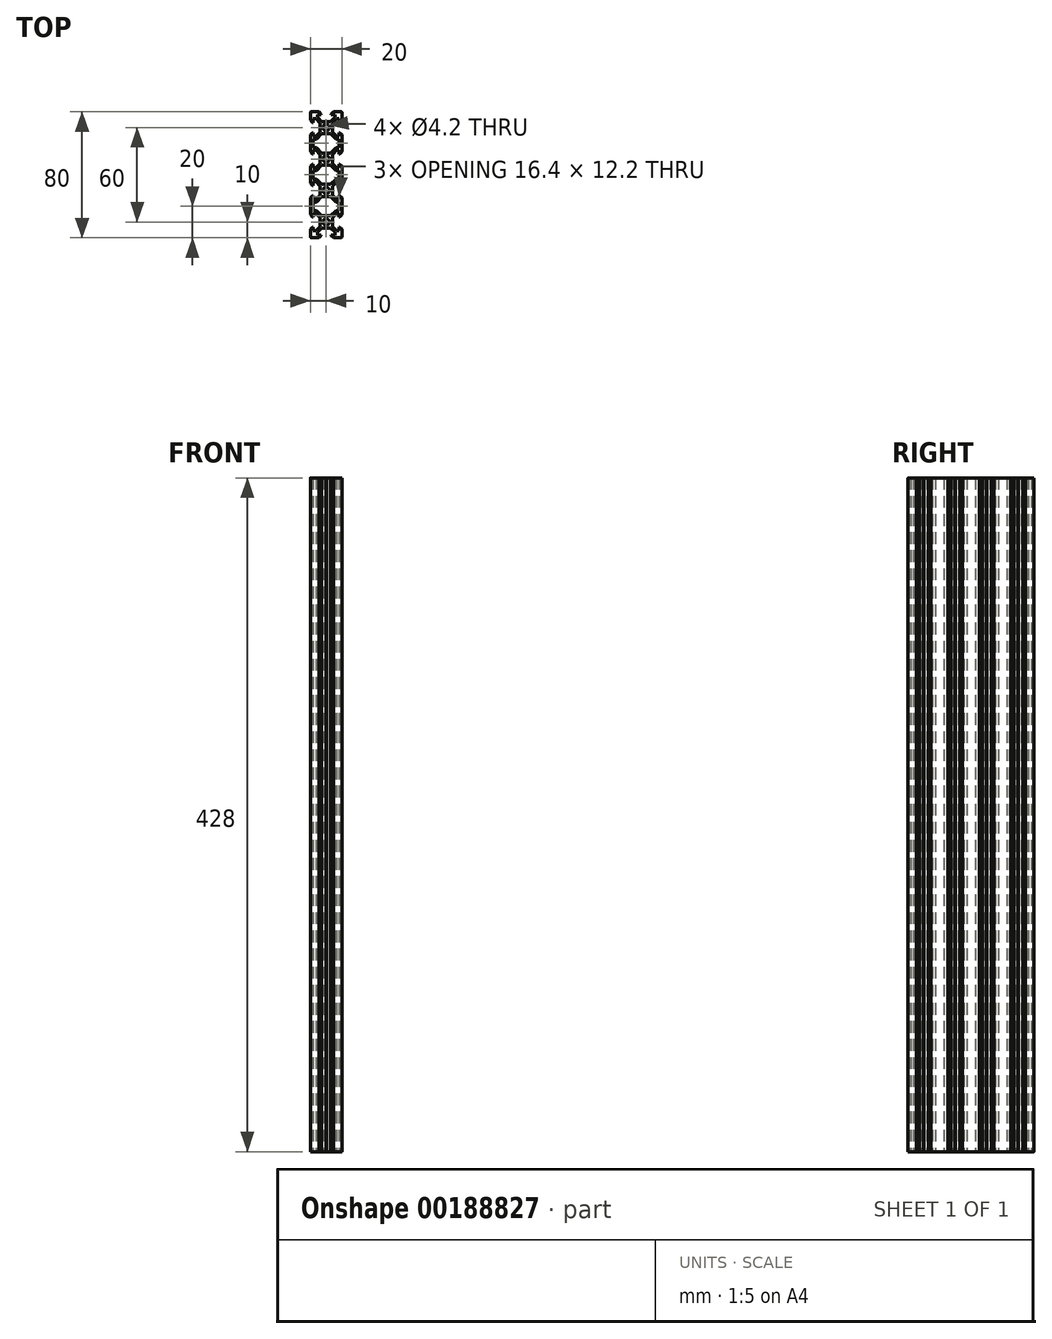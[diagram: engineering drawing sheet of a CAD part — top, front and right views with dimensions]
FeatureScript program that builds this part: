
annotation { "Feature Type Name" : "Feature", "Feature Type Description" : "" }
export const myFeature = defineFeature(function(context is Context, id is Id, definition is map)
    precondition{}
    {
        {
            assignVariable(context, id + "F0", {"name" : "altezza", "anyValue" : 428});
        }
        {
            var Q0;
            Q0=qCreatedBy(makeId("Top.planeOp"),FACE);
            var sketch = newSketch(context, id + "F1", { "sketchPlane" : qUnion([Q0])});
            skArc(sketch, "E0", {"start": v(-2.1, -10) * mm, "mid": v(0, -12.1) * mm, "end": v(2.1, -10) * mm});
            skArc(sketch, "E1", {"start": v(-2.1, -30) * mm, "mid": v(0, -32.1) * mm, "end": v(2.1, -30) * mm});
            skArc(sketch, "E2", {"start": v(-2.1, 30) * mm, "mid": v(0, 27.9) * mm, "end": v(2.1, 30) * mm});
            skArc(sketch, "E3", {"start": v(-2.1, 10) * mm, "mid": v(0, 7.9) * mm, "end": v(2.1, 10) * mm});
            skLineSegment(sketch, "E4", {"start": v(3.69, 30) * mm, "end": v(3.9, 29.79) * mm});
            skLineSegment(sketch, "E5", {"start": v(3.69, 30) * mm, "end": v(3.9, 30.21) * mm});
            skLineSegment(sketch, "E6", {"start": v(3.9, 30.21) * mm, "end": v(3.9, 32.84) * mm});
            skLineSegment(sketch, "E7", {"start": v(3.9, 32.84) * mm, "end": v(6.56, 35.5) * mm});
            skLineSegment(sketch, "E8", {"start": v(6.56, 35.5) * mm, "end": v(8.2, 35.5) * mm});
            skLineSegment(sketch, "E9", {"start": v(8.2, 35.5) * mm, "end": v(8.2, 33.12) * mm});
            skLineSegment(sketch, "E10", {"start": v(8.2, 33.12) * mm, "end": v(8.54, 33.12) * mm});
            skLineSegment(sketch, "E11", {"start": v(8.54, 33.12) * mm, "end": v(10, 34.58) * mm});
            skLineSegment(sketch, "E12", {"start": v(10, 34.58) * mm, "end": v(10, 39.5) * mm});
            skArc(sketch, "E13", {"start": v(10, 39.5) * mm, "mid": v(9.85, 39.85) * mm, "end": v(9.5, 40) * mm});
            skLineSegment(sketch, "E14", {"start": v(9.5, 40) * mm, "end": v(4.58, 40) * mm});
            skLineSegment(sketch, "E15", {"start": v(3.12, 38.55) * mm, "end": v(4.58, 40) * mm});
            skLineSegment(sketch, "E16", {"start": v(3.12, 38.2) * mm, "end": v(3.12, 38.55) * mm});
            skLineSegment(sketch, "E17", {"start": v(5.5, 38.2) * mm, "end": v(3.12, 38.2) * mm});
            skLineSegment(sketch, "E18", {"start": v(5.5, 36.56) * mm, "end": v(5.5, 38.2) * mm});
            skLineSegment(sketch, "E19", {"start": v(2.84, 33.9) * mm, "end": v(5.5, 36.56) * mm});
            skLineSegment(sketch, "E20", {"start": v(0.21, 33.9) * mm, "end": v(2.84, 33.9) * mm});
            skLineSegment(sketch, "E21", {"start": v(0, 33.69) * mm, "end": v(0.2, 33.9) * mm});
            skLineSegment(sketch, "E22", {"start": v(0, 33.69) * mm, "end": v(-0.2, 33.9) * mm});
            skLineSegment(sketch, "E23", {"start": v(-0.21, 33.9) * mm, "end": v(-2.84, 33.9) * mm});
            skLineSegment(sketch, "E24", {"start": v(-2.84, 33.9) * mm, "end": v(-5.5, 36.56) * mm});
            skLineSegment(sketch, "E25", {"start": v(-5.5, 36.56) * mm, "end": v(-5.5, 38.2) * mm});
            skLineSegment(sketch, "E26", {"start": v(-5.5, 38.2) * mm, "end": v(-3.12, 38.2) * mm});
            skLineSegment(sketch, "E27", {"start": v(-3.12, 38.2) * mm, "end": v(-3.12, 38.55) * mm});
            skLineSegment(sketch, "E28", {"start": v(-3.12, 38.55) * mm, "end": v(-4.58, 40) * mm});
            skLineSegment(sketch, "E29", {"start": v(-4.58, 40) * mm, "end": v(-9.5, 40) * mm});
            skArc(sketch, "E30", {"start": v(-9.5, 40) * mm, "mid": v(-9.85, 39.85) * mm, "end": v(-10, 39.5) * mm});
            skLineSegment(sketch, "E31", {"start": v(-10, 34.58) * mm, "end": v(-10, 39.5) * mm});
            skLineSegment(sketch, "E32", {"start": v(-8.54, 33.12) * mm, "end": v(-10, 34.58) * mm});
            skLineSegment(sketch, "E33", {"start": v(-8.2, 33.12) * mm, "end": v(-8.54, 33.12) * mm});
            skLineSegment(sketch, "E34", {"start": v(-8.2, 35.5) * mm, "end": v(-8.2, 33.12) * mm});
            skLineSegment(sketch, "E35", {"start": v(-6.56, 35.5) * mm, "end": v(-8.2, 35.5) * mm});
            skLineSegment(sketch, "E36", {"start": v(-3.9, 32.84) * mm, "end": v(-6.56, 35.5) * mm});
            skLineSegment(sketch, "E37", {"start": v(-3.9, 30.21) * mm, "end": v(-3.9, 32.84) * mm});
            skLineSegment(sketch, "E38", {"start": v(-3.69, 30) * mm, "end": v(-3.9, 30.21) * mm});
            skLineSegment(sketch, "E39", {"start": v(-3.69, 30) * mm, "end": v(-3.9, 29.79) * mm});
            skLineSegment(sketch, "E40", {"start": v(-3.9, 29.79) * mm, "end": v(-3.9, 27.16) * mm});
            skLineSegment(sketch, "E41", {"start": v(-3.9, 27.16) * mm, "end": v(-6.56, 24.5) * mm});
            skLineSegment(sketch, "E42", {"start": v(-6.56, 24.5) * mm, "end": v(-8.2, 24.5) * mm});
            skLineSegment(sketch, "E43", {"start": v(-8.2, 24.5) * mm, "end": v(-8.2, 26.88) * mm});
            skLineSegment(sketch, "E44", {"start": v(-8.2, 26.88) * mm, "end": v(-8.54, 26.88) * mm});
            skLineSegment(sketch, "E45", {"start": v(-8.54, 26.88) * mm, "end": v(-10, 25.42) * mm});
            skLineSegment(sketch, "E46", {"start": v(-10, 14.58) * mm, "end": v(-10, 25.42) * mm});
            skLineSegment(sketch, "E47", {"start": v(-8.54, 13.12) * mm, "end": v(-10, 14.58) * mm});
            skLineSegment(sketch, "E48", {"start": v(-8.2, 13.12) * mm, "end": v(-8.54, 13.12) * mm});
            skLineSegment(sketch, "E49", {"start": v(-8.2, 15.5) * mm, "end": v(-8.2, 13.12) * mm});
            skLineSegment(sketch, "E50", {"start": v(-6.56, 15.5) * mm, "end": v(-8.2, 15.5) * mm});
            skLineSegment(sketch, "E51", {"start": v(-3.9, 12.84) * mm, "end": v(-6.56, 15.5) * mm});
            skLineSegment(sketch, "E52", {"start": v(-3.9, 10.21) * mm, "end": v(-3.9, 12.84) * mm});
            skLineSegment(sketch, "E53", {"start": v(-3.69, 10) * mm, "end": v(-3.9, 10.21) * mm});
            skLineSegment(sketch, "E54", {"start": v(-3.69, 10) * mm, "end": v(-3.9, 9.8) * mm});
            skLineSegment(sketch, "E55", {"start": v(-3.9, 9.8) * mm, "end": v(-3.9, 7.16) * mm});
            skLineSegment(sketch, "E56", {"start": v(-3.9, 7.16) * mm, "end": v(-6.56, 4.5) * mm});
            skLineSegment(sketch, "E57", {"start": v(-6.56, 4.5) * mm, "end": v(-8.2, 4.5) * mm});
            skLineSegment(sketch, "E58", {"start": v(-8.2, 4.5) * mm, "end": v(-8.2, 6.88) * mm});
            skLineSegment(sketch, "E59", {"start": v(-8.2, 6.88) * mm, "end": v(-8.54, 6.88) * mm});
            skLineSegment(sketch, "E60", {"start": v(-8.54, 6.88) * mm, "end": v(-10, 5.42) * mm});
            skLineSegment(sketch, "E61", {"start": v(-10, -5.42) * mm, "end": v(-10, 5.42) * mm});
            skLineSegment(sketch, "E62", {"start": v(-8.54, -6.88) * mm, "end": v(-10, -5.42) * mm});
            skLineSegment(sketch, "E63", {"start": v(-8.2, -6.88) * mm, "end": v(-8.54, -6.88) * mm});
            skLineSegment(sketch, "E64", {"start": v(-8.2, -4.5) * mm, "end": v(-8.2, -6.88) * mm});
            skLineSegment(sketch, "E65", {"start": v(-6.56, -4.5) * mm, "end": v(-8.2, -4.5) * mm});
            skLineSegment(sketch, "E66", {"start": v(-3.9, -7.16) * mm, "end": v(-6.56, -4.5) * mm});
            skLineSegment(sketch, "E67", {"start": v(-3.9, -9.8) * mm, "end": v(-3.9, -7.16) * mm});
            skLineSegment(sketch, "E68", {"start": v(-3.69, -10) * mm, "end": v(-3.9, -9.8) * mm});
            skLineSegment(sketch, "E69", {"start": v(-3.69, -10) * mm, "end": v(-3.9, -10.21) * mm});
            skLineSegment(sketch, "E70", {"start": v(-3.9, -10.21) * mm, "end": v(-3.9, -12.84) * mm});
            skLineSegment(sketch, "E71", {"start": v(-3.9, -12.84) * mm, "end": v(-6.56, -15.5) * mm});
            skLineSegment(sketch, "E72", {"start": v(-6.56, -15.5) * mm, "end": v(-8.2, -15.5) * mm});
            skLineSegment(sketch, "E73", {"start": v(-8.2, -15.5) * mm, "end": v(-8.2, -13.12) * mm});
            skLineSegment(sketch, "E74", {"start": v(-8.2, -13.12) * mm, "end": v(-8.54, -13.12) * mm});
            skLineSegment(sketch, "E75", {"start": v(-8.54, -13.12) * mm, "end": v(-10, -14.58) * mm});
            skLineSegment(sketch, "E76", {"start": v(-10, -25.42) * mm, "end": v(-10, -14.58) * mm});
            skLineSegment(sketch, "E77", {"start": v(-8.54, -26.88) * mm, "end": v(-10, -25.42) * mm});
            skLineSegment(sketch, "E78", {"start": v(-8.2, -26.88) * mm, "end": v(-8.54, -26.88) * mm});
            skLineSegment(sketch, "E79", {"start": v(-8.2, -24.5) * mm, "end": v(-8.2, -26.88) * mm});
            skLineSegment(sketch, "E80", {"start": v(-6.56, -24.5) * mm, "end": v(-8.2, -24.5) * mm});
            skLineSegment(sketch, "E81", {"start": v(-3.9, -27.16) * mm, "end": v(-6.56, -24.5) * mm});
            skLineSegment(sketch, "E82", {"start": v(-3.9, -29.79) * mm, "end": v(-3.9, -27.16) * mm});
            skLineSegment(sketch, "E83", {"start": v(-3.69, -30) * mm, "end": v(-3.9, -29.79) * mm});
            skLineSegment(sketch, "E84", {"start": v(-3.69, -30) * mm, "end": v(-3.9, -30.21) * mm});
            skLineSegment(sketch, "E85", {"start": v(-3.9, -30.21) * mm, "end": v(-3.9, -32.84) * mm});
            skLineSegment(sketch, "E86", {"start": v(-3.9, -32.84) * mm, "end": v(-6.56, -35.5) * mm});
            skLineSegment(sketch, "E87", {"start": v(-6.56, -35.5) * mm, "end": v(-8.2, -35.5) * mm});
            skLineSegment(sketch, "E88", {"start": v(-8.2, -35.5) * mm, "end": v(-8.2, -33.12) * mm});
            skLineSegment(sketch, "E89", {"start": v(-8.2, -33.12) * mm, "end": v(-8.54, -33.12) * mm});
            skLineSegment(sketch, "E90", {"start": v(-8.54, -33.12) * mm, "end": v(-10, -34.58) * mm});
            skLineSegment(sketch, "E91", {"start": v(-10, -39.5) * mm, "end": v(-10, -34.58) * mm});
            skArc(sketch, "E92", {"start": v(-10, -39.5) * mm, "mid": v(-9.85, -39.85) * mm, "end": v(-9.5, -40) * mm});
            skLineSegment(sketch, "E93", {"start": v(-4.58, -40) * mm, "end": v(-9.5, -40) * mm});
            skLineSegment(sketch, "E94", {"start": v(-3.12, -38.55) * mm, "end": v(-4.58, -40) * mm});
            skLineSegment(sketch, "E95", {"start": v(-3.12, -38.2) * mm, "end": v(-3.12, -38.55) * mm});
            skLineSegment(sketch, "E96", {"start": v(-5.5, -38.2) * mm, "end": v(-3.12, -38.2) * mm});
            skLineSegment(sketch, "E97", {"start": v(-5.5, -36.56) * mm, "end": v(-5.5, -38.2) * mm});
            skLineSegment(sketch, "E98", {"start": v(-2.84, -33.9) * mm, "end": v(-5.5, -36.56) * mm});
            skLineSegment(sketch, "E99", {"start": v(-0.21, -33.9) * mm, "end": v(-2.84, -33.9) * mm});
            skLineSegment(sketch, "E100", {"start": v(0, -33.69) * mm, "end": v(-0.2, -33.9) * mm});
            skLineSegment(sketch, "E101", {"start": v(0, -33.69) * mm, "end": v(0.2, -33.9) * mm});
            skLineSegment(sketch, "E102", {"start": v(0.21, -33.9) * mm, "end": v(2.84, -33.9) * mm});
            skLineSegment(sketch, "E103", {"start": v(2.84, -33.9) * mm, "end": v(5.5, -36.56) * mm});
            skLineSegment(sketch, "E104", {"start": v(5.5, -36.56) * mm, "end": v(5.5, -38.2) * mm});
            skLineSegment(sketch, "E105", {"start": v(5.5, -38.2) * mm, "end": v(3.12, -38.2) * mm});
            skLineSegment(sketch, "E106", {"start": v(3.12, -38.2) * mm, "end": v(3.12, -38.55) * mm});
            skLineSegment(sketch, "E107", {"start": v(3.12, -38.55) * mm, "end": v(4.58, -40) * mm});
            skLineSegment(sketch, "E108", {"start": v(9.5, -40) * mm, "end": v(4.58, -40) * mm});
            skArc(sketch, "E109", {"start": v(9.5, -40) * mm, "mid": v(9.85, -39.85) * mm, "end": v(10, -39.5) * mm});
            skLineSegment(sketch, "E110", {"start": v(10, -39.5) * mm, "end": v(10, -34.58) * mm});
            skLineSegment(sketch, "E111", {"start": v(8.54, -33.12) * mm, "end": v(10, -34.58) * mm});
            skLineSegment(sketch, "E112", {"start": v(8.2, -33.12) * mm, "end": v(8.54, -33.12) * mm});
            skLineSegment(sketch, "E113", {"start": v(8.2, -35.5) * mm, "end": v(8.2, -33.12) * mm});
            skLineSegment(sketch, "E114", {"start": v(6.56, -35.5) * mm, "end": v(8.2, -35.5) * mm});
            skLineSegment(sketch, "E115", {"start": v(3.9, -32.84) * mm, "end": v(6.56, -35.5) * mm});
            skLineSegment(sketch, "E116", {"start": v(3.9, -30.21) * mm, "end": v(3.9, -32.84) * mm});
            skLineSegment(sketch, "E117", {"start": v(3.69, -30) * mm, "end": v(3.9, -30.21) * mm});
            skLineSegment(sketch, "E118", {"start": v(3.69, -30) * mm, "end": v(3.9, -29.79) * mm});
            skLineSegment(sketch, "E119", {"start": v(3.9, -29.79) * mm, "end": v(3.9, -27.16) * mm});
            skLineSegment(sketch, "E120", {"start": v(3.9, -27.16) * mm, "end": v(6.56, -24.5) * mm});
            skLineSegment(sketch, "E121", {"start": v(6.56, -24.5) * mm, "end": v(8.2, -24.5) * mm});
            skLineSegment(sketch, "E122", {"start": v(8.2, -24.5) * mm, "end": v(8.2, -26.88) * mm});
            skLineSegment(sketch, "E123", {"start": v(8.2, -26.88) * mm, "end": v(8.54, -26.88) * mm});
            skLineSegment(sketch, "E124", {"start": v(8.54, -26.88) * mm, "end": v(10, -25.42) * mm});
            skLineSegment(sketch, "E125", {"start": v(10, -25.42) * mm, "end": v(10, -14.58) * mm});
            skLineSegment(sketch, "E126", {"start": v(8.54, -13.12) * mm, "end": v(10, -14.58) * mm});
            skLineSegment(sketch, "E127", {"start": v(8.2, -13.12) * mm, "end": v(8.54, -13.12) * mm});
            skLineSegment(sketch, "E128", {"start": v(8.2, -15.5) * mm, "end": v(8.2, -13.12) * mm});
            skLineSegment(sketch, "E129", {"start": v(6.56, -15.5) * mm, "end": v(8.2, -15.5) * mm});
            skLineSegment(sketch, "E130", {"start": v(3.9, -12.84) * mm, "end": v(6.56, -15.5) * mm});
            skLineSegment(sketch, "E131", {"start": v(3.9, -10.21) * mm, "end": v(3.9, -12.84) * mm});
            skLineSegment(sketch, "E132", {"start": v(3.69, -10) * mm, "end": v(3.9, -10.21) * mm});
            skLineSegment(sketch, "E133", {"start": v(3.69, -10) * mm, "end": v(3.9, -9.8) * mm});
            skLineSegment(sketch, "E134", {"start": v(3.9, -9.8) * mm, "end": v(3.9, -7.16) * mm});
            skLineSegment(sketch, "E135", {"start": v(3.9, -7.16) * mm, "end": v(6.56, -4.5) * mm});
            skLineSegment(sketch, "E136", {"start": v(6.56, -4.5) * mm, "end": v(8.2, -4.5) * mm});
            skLineSegment(sketch, "E137", {"start": v(8.2, -4.5) * mm, "end": v(8.2, -6.88) * mm});
            skLineSegment(sketch, "E138", {"start": v(8.2, -6.88) * mm, "end": v(8.54, -6.88) * mm});
            skLineSegment(sketch, "E139", {"start": v(8.54, -6.88) * mm, "end": v(10, -5.42) * mm});
            skLineSegment(sketch, "E140", {"start": v(10, -5.42) * mm, "end": v(10, 5.42) * mm});
            skLineSegment(sketch, "E141", {"start": v(8.54, 6.88) * mm, "end": v(10, 5.42) * mm});
            skLineSegment(sketch, "E142", {"start": v(8.2, 6.88) * mm, "end": v(8.54, 6.88) * mm});
            skLineSegment(sketch, "E143", {"start": v(8.2, 4.5) * mm, "end": v(8.2, 6.88) * mm});
            skLineSegment(sketch, "E144", {"start": v(6.56, 4.5) * mm, "end": v(8.2, 4.5) * mm});
            skLineSegment(sketch, "E145", {"start": v(3.9, 7.16) * mm, "end": v(6.56, 4.5) * mm});
            skLineSegment(sketch, "E146", {"start": v(3.9, 9.8) * mm, "end": v(3.9, 7.16) * mm});
            skLineSegment(sketch, "E147", {"start": v(3.69, 10) * mm, "end": v(3.9, 9.8) * mm});
            skLineSegment(sketch, "E148", {"start": v(3.69, 10) * mm, "end": v(3.9, 10.21) * mm});
            skLineSegment(sketch, "E149", {"start": v(3.9, 10.21) * mm, "end": v(3.9, 12.84) * mm});
            skLineSegment(sketch, "E150", {"start": v(3.9, 12.84) * mm, "end": v(6.56, 15.5) * mm});
            skLineSegment(sketch, "E151", {"start": v(6.56, 15.5) * mm, "end": v(8.2, 15.5) * mm});
            skLineSegment(sketch, "E152", {"start": v(8.2, 15.5) * mm, "end": v(8.2, 13.12) * mm});
            skLineSegment(sketch, "E153", {"start": v(8.2, 13.12) * mm, "end": v(8.54, 13.12) * mm});
            skLineSegment(sketch, "E154", {"start": v(8.54, 13.12) * mm, "end": v(10, 14.58) * mm});
            skLineSegment(sketch, "E155", {"start": v(10, 14.58) * mm, "end": v(10, 25.42) * mm});
            skLineSegment(sketch, "E156", {"start": v(8.54, 26.88) * mm, "end": v(10, 25.42) * mm});
            skLineSegment(sketch, "E157", {"start": v(8.2, 26.88) * mm, "end": v(8.54, 26.88) * mm});
            skLineSegment(sketch, "E158", {"start": v(8.2, 24.5) * mm, "end": v(8.2, 26.88) * mm});
            skLineSegment(sketch, "E159", {"start": v(6.56, 24.5) * mm, "end": v(8.2, 24.5) * mm});
            skLineSegment(sketch, "E160", {"start": v(3.9, 27.16) * mm, "end": v(6.56, 24.5) * mm});
            skLineSegment(sketch, "E161", {"start": v(-8.2, 17.3) * mm, "end": v(-6.24, 17.3) * mm});
            skLineSegment(sketch, "E162", {"start": v(-8.2, 17.3) * mm, "end": v(-8.2, 22.7) * mm});
            skLineSegment(sketch, "E163", {"start": v(-8.2, 22.7) * mm, "end": v(-6.24, 22.7) * mm});
            skLineSegment(sketch, "E164", {"start": v(-6.24, 22.7) * mm, "end": v(-2.84, 26.1) * mm});
            skLineSegment(sketch, "E165", {"start": v(-2.84, 26.1) * mm, "end": v(2.84, 26.1) * mm});
            skLineSegment(sketch, "E166", {"start": v(6.24, 22.7) * mm, "end": v(2.84, 26.1) * mm});
            skLineSegment(sketch, "E167", {"start": v(8.2, 22.7) * mm, "end": v(6.24, 22.7) * mm});
            skLineSegment(sketch, "E168", {"start": v(8.2, 17.3) * mm, "end": v(8.2, 22.7) * mm});
            skLineSegment(sketch, "E169", {"start": v(8.2, 17.3) * mm, "end": v(6.24, 17.3) * mm});
            skLineSegment(sketch, "E170", {"start": v(6.24, 17.3) * mm, "end": v(2.84, 13.9) * mm});
            skLineSegment(sketch, "E171", {"start": v(-2.84, 13.9) * mm, "end": v(2.84, 13.9) * mm});
            skLineSegment(sketch, "E172", {"start": v(-8.2, -2.7) * mm, "end": v(-6.24, -2.7) * mm});
            skLineSegment(sketch, "E173", {"start": v(-8.2, -2.7) * mm, "end": v(-8.2, 2.7) * mm});
            skLineSegment(sketch, "E174", {"start": v(-8.2, 2.7) * mm, "end": v(-6.24, 2.7) * mm});
            skLineSegment(sketch, "E175", {"start": v(-6.24, 2.7) * mm, "end": v(-2.84, 6.1) * mm});
            skLineSegment(sketch, "E176", {"start": v(-2.84, 6.1) * mm, "end": v(2.84, 6.1) * mm});
            skLineSegment(sketch, "E177", {"start": v(6.24, 2.7) * mm, "end": v(2.84, 6.1) * mm});
            skLineSegment(sketch, "E178", {"start": v(8.2, 2.7) * mm, "end": v(6.24, 2.7) * mm});
            skLineSegment(sketch, "E179", {"start": v(8.2, -2.7) * mm, "end": v(8.2, 2.7) * mm});
            skLineSegment(sketch, "E180", {"start": v(8.2, -2.7) * mm, "end": v(6.24, -2.7) * mm});
            skLineSegment(sketch, "E181", {"start": v(6.24, -2.7) * mm, "end": v(2.84, -6.1) * mm});
            skLineSegment(sketch, "E182", {"start": v(-2.84, -6.1) * mm, "end": v(2.84, -6.1) * mm});
            skLineSegment(sketch, "E183", {"start": v(-8.2, -22.7) * mm, "end": v(-6.24, -22.7) * mm});
            skLineSegment(sketch, "E184", {"start": v(-8.2, -22.7) * mm, "end": v(-8.2, -17.3) * mm});
            skLineSegment(sketch, "E185", {"start": v(-8.2, -17.3) * mm, "end": v(-6.24, -17.3) * mm});
            skLineSegment(sketch, "E186", {"start": v(-6.24, -17.3) * mm, "end": v(-2.84, -13.9) * mm});
            skLineSegment(sketch, "E187", {"start": v(-2.84, -13.9) * mm, "end": v(2.84, -13.9) * mm});
            skLineSegment(sketch, "E188", {"start": v(6.24, -17.3) * mm, "end": v(2.84, -13.9) * mm});
            skLineSegment(sketch, "E189", {"start": v(8.2, -17.3) * mm, "end": v(6.24, -17.3) * mm});
            skLineSegment(sketch, "E190", {"start": v(8.2, -22.7) * mm, "end": v(8.2, -17.3) * mm});
            skLineSegment(sketch, "E191", {"start": v(8.2, -22.7) * mm, "end": v(6.24, -22.7) * mm});
            skLineSegment(sketch, "E192", {"start": v(6.24, -22.7) * mm, "end": v(2.84, -26.1) * mm});
            skLineSegment(sketch, "E193", {"start": v(-2.84, -26.1) * mm, "end": v(2.84, -26.1) * mm});
            skArc(sketch, "E194", {"start": v(2.1, 10) * mm, "mid": v(0, 12.1) * mm, "end": v(-2.1, 10) * mm});
            skArc(sketch, "E195", {"start": v(2.1, 30) * mm, "mid": v(0, 32.1) * mm, "end": v(-2.1, 30) * mm});
            skArc(sketch, "E196", {"start": v(2.1, -30) * mm, "mid": v(0, -27.9) * mm, "end": v(-2.1, -30) * mm});
            skLineSegment(sketch, "E197", {"start": v(3.9, 29.79) * mm, "end": v(3.9, 27.16) * mm});
            skLineSegment(sketch, "E198", {"start": v(-6.24, 17.3) * mm, "end": v(-2.84, 13.9) * mm});
            skLineSegment(sketch, "E199", {"start": v(-6.24, -2.7) * mm, "end": v(-2.84, -6.1) * mm});
            skLineSegment(sketch, "E200", {"start": v(-6.24, -22.7) * mm, "end": v(-2.84, -26.1) * mm});
            skArc(sketch, "E201", {"start": v(2.1, -10) * mm, "mid": v(0, -7.9) * mm, "end": v(-2.1, -10) * mm});
            skSolve(sketch);
        }
        {
            var Q0;
            Q0=makeQuery(id+"F1.imprint","IMPRINT",FACE,{"disambiguationData":[TD([[makeQuery(id+"F1.imprint","IMPRINT",EDGE,{"derivedFrom":sQuery(id+"F1.wireOp",EDGE,"E0")}),-1.0]])]});
            extrude(context, id + "F2", {"entities" : qUnion([Q0]), "depth" : (getVariable(context, 'altezza')) * mm, "offsetDistance" : 25 * mm});
        }
    });
